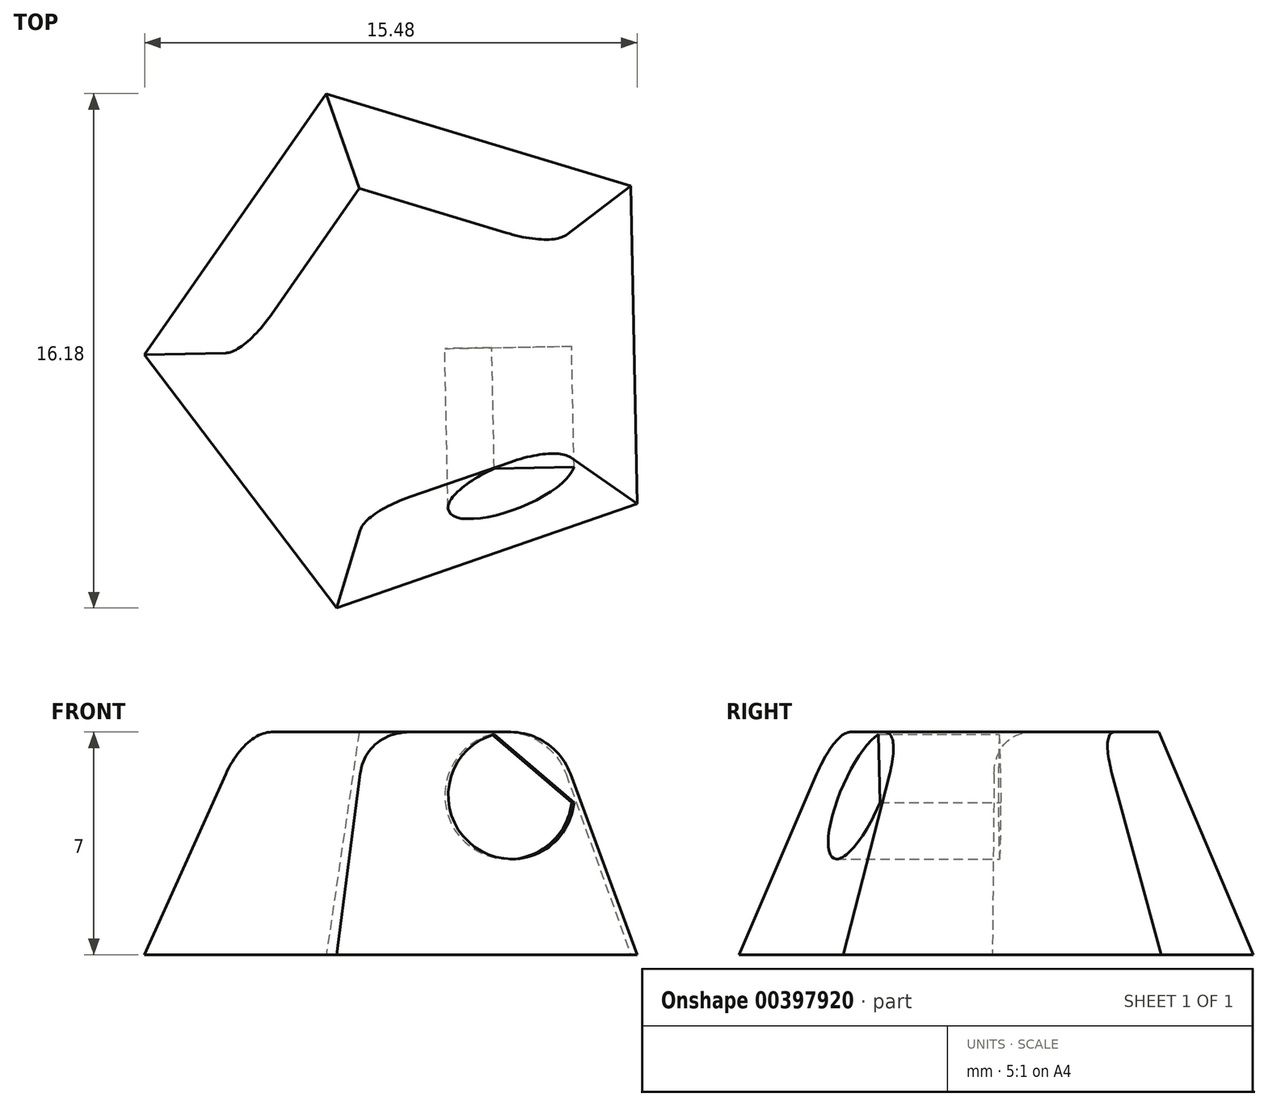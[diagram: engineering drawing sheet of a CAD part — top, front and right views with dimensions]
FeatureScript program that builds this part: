
annotation { "Feature Type Name" : "Feature", "Feature Type Description" : "" }
export const myFeature = defineFeature(function(context is Context, id is Id, definition is map)
    precondition{}
    {
        {
            var Q0;
            Q0=qCreatedBy(makeId("Top.planeOp"),FACE);
            var sketch = newSketch(context, id + "F0", { "sketchPlane" : qUnion([Q0])});
            skCircle(sketch, "E0.cCircle", {"center": v(0, 0) * mm, "radius": 8.5 * mm, "construction": true});
            skLineSegment(sketch, "E0.0", {"start": v(6.98, -4.86) * mm, "end": v(-2.47, -8.14) * mm});
            skLineSegment(sketch, "E0.1", {"start": v(-2.47, -8.14) * mm, "end": v(-8.5, -0.17) * mm});
            skLineSegment(sketch, "E0.2", {"start": v(-8.5, -0.17) * mm, "end": v(-2.79, 8.04) * mm});
            skLineSegment(sketch, "E0.3", {"start": v(-2.79, 8.04) * mm, "end": v(6.78, 5.14) * mm});
            skLineSegment(sketch, "E0.4", {"start": v(6.78, 5.14) * mm, "end": v(6.98, -4.86) * mm});
            skSolve(sketch);
        }
        {
            var Q0;
            Q0=makeQuery(id+"F0.imprint","IMPRINT",FACE,{"disambiguationData":[TD([[makeQuery(id+"F0.imprint","IMPRINT",EDGE,{"derivedFrom":sQuery(id+"F0.wireOp",EDGE,"E0.0")}),-1.0]])]});
            extrude(context, id + "F1", {"entities" : qUnion([Q0]), "depth" : 7 * mm, "hasDraft" : true, "draftAngle" : 20 * degree, "draftPullDirection" : true});
        }
        {
            var Q0;
            Q0=makeQuery(id+"F1.opExtrude","CAP_EDGE",EDGE,{"disambiguationData":[OSD([sQuery(id+"F0.wireOp",EDGE,"E0.4")])],"isStart":false});
            var Q1;
            Q1=makeQuery(id+"F1.opExtrude","CAP_EDGE",EDGE,{"disambiguationData":[OSD([sQuery(id+"F0.wireOp",EDGE,"E0.1")])],"isStart":false});
            fillet(context, id + "F2", {"entities" : qUnion([Q0, Q1]), "radius" : 2 * mm, "tangentPropagation" : true, "allowEdgeOverflow" : false});
        }
        {
            var Q0;
            {var subQ0=sQuery(id+"F0.wireOp",EDGE,"E0.4");Q0=makeQuery(id+"F2.opFillet","BLEND_EDGE",EDGE,{"blendedFrom":[makeQuery(id+"F1.opExtrude","CAP_EDGE",EDGE,{"disambiguationData":[OSD([subQ0])],"isStart":false}),makeQuery(id+"F1.opExtrude","CAP_FACE",FACE,{"disambiguationData":[OSD([sQuery(id+"F0.wireOp",EDGE,"E0.0"),sQuery(id+"F0.wireOp",EDGE,"E0.1"),sQuery(id+"F0.wireOp",EDGE,"E0.2"),sQuery(id+"F0.wireOp",EDGE,"E0.3"),subQ0])],"isStart":false})],"blendedInto":[makeQuery(id+"F1.opExtrude","CAP_FACE",FACE,{"disambiguationData":[OSD([sQuery(id+"F0.wireOp",EDGE,"E0.0"),sQuery(id+"F0.wireOp",EDGE,"E0.1"),sQuery(id+"F0.wireOp",EDGE,"E0.2"),sQuery(id+"F0.wireOp",EDGE,"E0.3"),subQ0])],"isStart":false})]});}
            cPoint(context, id + "F3", {"entities" : qUnion([Q0]), "parameter" : 0.5});
        }
        {
            var Q0;
            Q0 = qCreatedBy(id + "F3" ,VERTEX);
            var Q1;
            {var subQ0=sQuery(id+"F0.wireOp",EDGE,"E0.4");Q1=makeQuery(id+"F2.opFillet","BLEND_EDGE",EDGE,{"blendedFrom":[makeQuery(id+"F1.opExtrude","CAP_EDGE",EDGE,{"disambiguationData":[OSD([subQ0])],"isStart":false}),makeQuery(id+"F1.opExtrude","CAP_FACE",FACE,{"disambiguationData":[OSD([sQuery(id+"F0.wireOp",EDGE,"E0.0"),sQuery(id+"F0.wireOp",EDGE,"E0.1"),sQuery(id+"F0.wireOp",EDGE,"E0.2"),sQuery(id+"F0.wireOp",EDGE,"E0.3"),subQ0])],"isStart":false})],"blendedInto":[makeQuery(id+"F1.opExtrude","CAP_FACE",FACE,{"disambiguationData":[OSD([sQuery(id+"F0.wireOp",EDGE,"E0.0"),sQuery(id+"F0.wireOp",EDGE,"E0.1"),sQuery(id+"F0.wireOp",EDGE,"E0.2"),sQuery(id+"F0.wireOp",EDGE,"E0.3"),subQ0])],"isStart":false})]});}
            cPlane(context, id + "F4", {"entities" : qUnion([Q0, Q1]), "cplaneType" : CPlaneType.LINE_POINT, "offset" : 25 * mm, "width" : 150 * mm, "height" : 150 * mm});
        }
        {
            var Q0;
            Q0=qCreatedBy(id+"F4.planeOp",FACE);
            var sketch = newSketch(context, id + "F5", { "sketchPlane" : qUnion([Q0])});
            skLineSegment(sketch, "E1", {"start": v(2.41, 6.93) * mm, "end": v(4.92, 4.78) * mm});
            skPoint(sketch, "E2.0.end.orphan", {"position": v(2.93, 7) * mm});
            skPoint(sketch, "E2.0.start.orphan", {"position": v(4.81, 5.68) * mm});
            skArc(sketch, "E3.trimOffspring", {"start": v(2.41, 6.93) * mm, "mid": v(1.63, 3.48) * mm, "end": v(4.92, 4.78) * mm});
            skSolve(sketch);
        }
        {
            var Q0;
            Q0 = qSketchRegion(id + "F5", true);
            extrude(context, id + "F6", {"entities" : qUnion([Q0]), "operationType" : NewBodyOperationType.REMOVE, "endBound" : BoundingType.UP_TO_NEXT, "depth" : 25 * mm});
        }
    });
